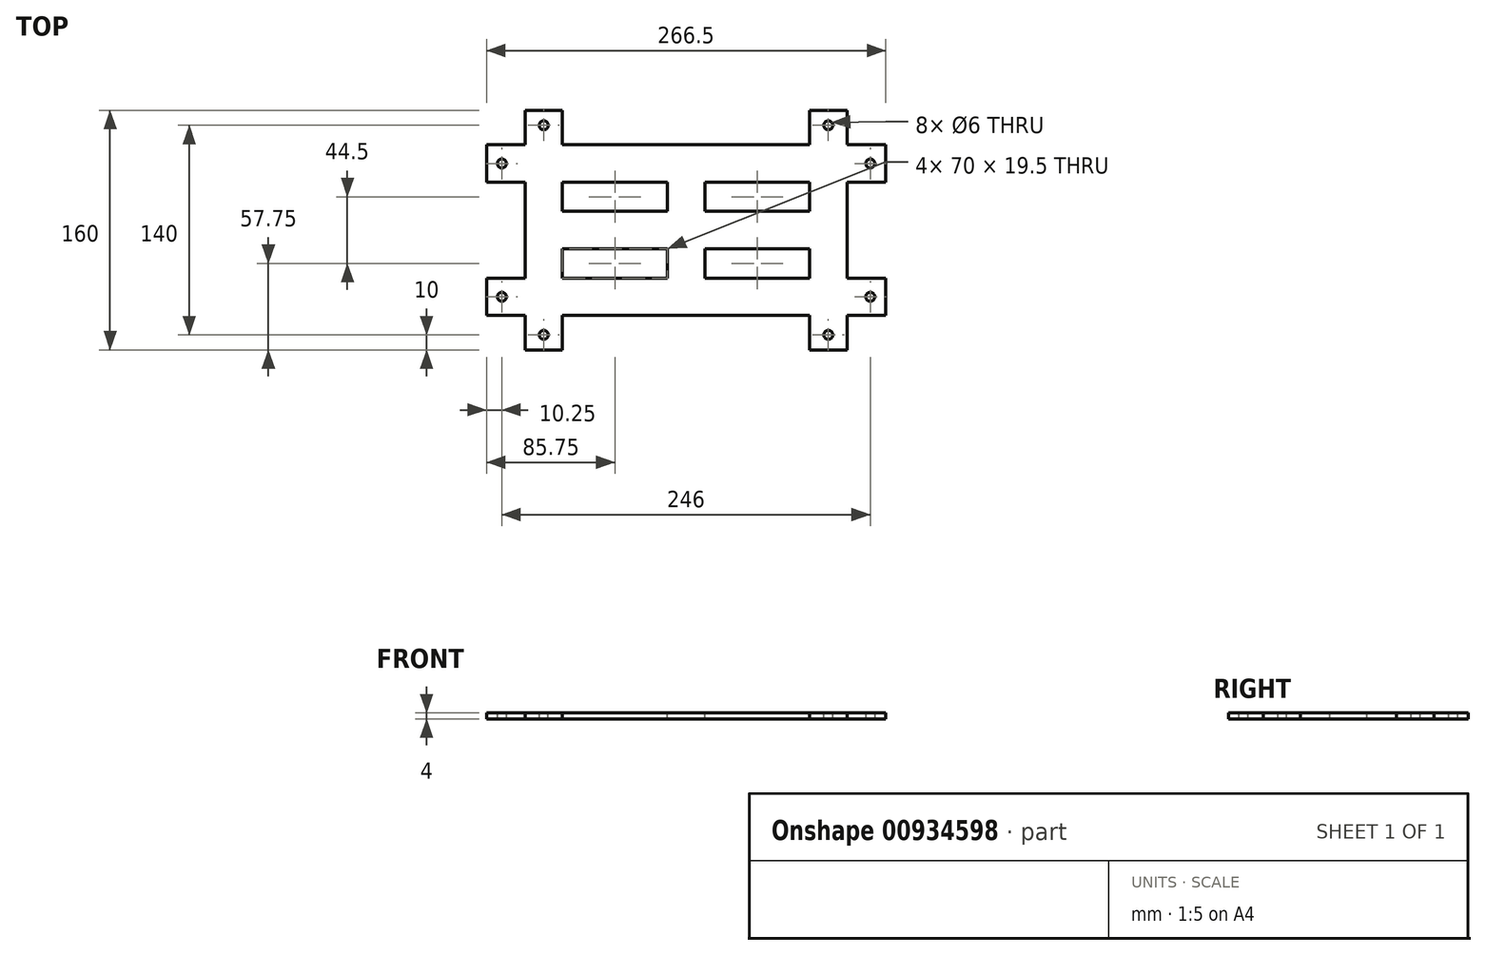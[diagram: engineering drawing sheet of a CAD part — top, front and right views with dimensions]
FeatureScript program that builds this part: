
annotation { "Feature Type Name" : "Feature", "Feature Type Description" : "" }
export const myFeature = defineFeature(function(context is Context, id is Id, definition is map)
    precondition{}
    {
        {
            var Q0;
            Q0=qCreatedBy(makeId("Top.planeOp"),FACE);
            var sketch = newSketch(context, id + "F0", { "sketchPlane" : qUnion([Q0])});
            skLineSegment(sketch, "E0.bottom", {"start": v(-133.25, 80) * mm, "end": v(133.25, 80) * mm});
            skLineSegment(sketch, "E0.top", {"start": v(-133.25, -80) * mm, "end": v(133.25, -80) * mm});
            skLineSegment(sketch, "E0.left", {"start": v(-133.25, 80) * mm, "end": v(-133.25, -80) * mm});
            skLineSegment(sketch, "E0.right", {"start": v(133.25, 80) * mm, "end": v(133.25, -80) * mm});
            skCircle(sketch, "E1", {"center": v(-123, 44.5) * mm, "radius": 3 * mm});
            skCircle(sketch, "E2", {"center": v(-123, -44.5) * mm, "radius": 3 * mm});
            skCircle(sketch, "E3", {"center": v(123, -44.5) * mm, "radius": 3 * mm});
            skCircle(sketch, "E4", {"center": v(123, 44.5) * mm, "radius": 3 * mm});
            skSolve(sketch);
        }
        {
            var Q0;
            Q0 = qSketchRegion(id + "F0", true);
            extrude(context, id + "F1", {"entities" : qUnion([Q0]), "depth" : 4 * mm, "offsetDistance" : 25 * mm});
        }
        {
            var Q0;
            Q0=makeQuery(id+"F1.opExtrude","CAP_FACE",FACE,{"disambiguationData":[OSD([sQuery(id+"F0.wireOp",EDGE,"E0.bottom"),sQuery(id+"F0.wireOp",EDGE,"E0.top"),sQuery(id+"F0.wireOp",EDGE,"E0.left"),sQuery(id+"F0.wireOp",EDGE,"E0.right"),sQuery(id+"F0.wireOp",EDGE,"E1"),sQuery(id+"F0.wireOp",EDGE,"E2"),sQuery(id+"F0.wireOp",EDGE,"E3"),sQuery(id+"F0.wireOp",EDGE,"E4")])],"isStart":false});
            var sketch = newSketch(context, id + "F2", { "sketchPlane" : qUnion([Q0])});
            skCircle(sketch, "E5", {"center": v(-95, 70) * mm, "radius": 3 * mm});
            skCircle(sketch, "E6", {"center": v(-95, -70) * mm, "radius": 3 * mm});
            skCircle(sketch, "E7.MirrorC", {"center": v(95, 70) * mm, "radius": 3 * mm});
            skCircle(sketch, "E8.MirrorC", {"center": v(95, -70) * mm, "radius": 3 * mm});
            skSolve(sketch);
        }
        {
            var Q0;
            Q0 = qSketchRegion(id + "F2", true);
            extrude(context, id + "F3", {"entities" : qUnion([Q0]), "operationType" : NewBodyOperationType.REMOVE, "endBound" : BoundingType.THROUGH_ALL, "oppositeDirection" : true, "depth" : 25 * mm, "offsetDistance" : 25 * mm});
        }
        {
            var Q0;
            Q0=makeQuery(id+"F1.opExtrude","CAP_FACE",FACE,{"disambiguationData":[OSD([sQuery(id+"F0.wireOp",EDGE,"E0.bottom"),sQuery(id+"F0.wireOp",EDGE,"E0.top"),sQuery(id+"F0.wireOp",EDGE,"E0.left"),sQuery(id+"F0.wireOp",EDGE,"E0.right"),sQuery(id+"F0.wireOp",EDGE,"E1"),sQuery(id+"F0.wireOp",EDGE,"E2"),sQuery(id+"F0.wireOp",EDGE,"E3"),sQuery(id+"F0.wireOp",EDGE,"E4")])],"isStart":false});
            var sketch = newSketch(context, id + "F4", { "sketchPlane" : qUnion([Q0])});
            skLineSegment(sketch, "E9.bottom", {"start": v(-133.25, 80) * mm, "end": v(-107.5, 80) * mm});
            skLineSegment(sketch, "E9.top", {"start": v(-133.25, 57) * mm, "end": v(-107.5, 57) * mm});
            skLineSegment(sketch, "E9.left", {"start": v(-133.25, 80) * mm, "end": v(-133.25, 57) * mm});
            skLineSegment(sketch, "E9.right", {"start": v(-107.5, 80) * mm, "end": v(-107.5, 57) * mm});
            skLineSegment(sketch, "E10.bottom", {"start": v(-82.5, 80) * mm, "end": v(0, 80) * mm});
            skLineSegment(sketch, "E10.top", {"start": v(-82.5, 57) * mm, "end": v(0, 57) * mm});
            skLineSegment(sketch, "E10.left", {"start": v(-82.5, 80) * mm, "end": v(-82.5, 57) * mm});
            skLineSegment(sketch, "E10.right", {"start": v(0, 80) * mm, "end": v(0, 57) * mm});
            skLineSegment(sketch, "E11.bottom", {"start": v(-107.5, 32) * mm, "end": v(-133.25, 32) * mm});
            skLineSegment(sketch, "E11.top", {"start": v(-107.5, 0) * mm, "end": v(-133.25, 0) * mm});
            skLineSegment(sketch, "E11.left", {"start": v(-107.5, 32) * mm, "end": v(-107.5, 0) * mm});
            skLineSegment(sketch, "E11.right", {"start": v(-133.25, 32) * mm, "end": v(-133.25, 0) * mm});
            skLineSegment(sketch, "E12.MirrorCS", {"start": v(133.25, 80) * mm, "end": v(133.25, 57) * mm});
            skLineSegment(sketch, "E13.MirrorCS", {"start": v(82.5, 57) * mm, "end": v(0, 57) * mm});
            skLineSegment(sketch, "E14.MirrorCS", {"start": v(133.25, 57) * mm, "end": v(107.5, 57) * mm});
            skLineSegment(sketch, "E15.MirrorCS", {"start": v(82.5, 80) * mm, "end": v(0, 80) * mm});
            skLineSegment(sketch, "E16.MirrorCS", {"start": v(107.5, 80) * mm, "end": v(107.5, 57) * mm});
            skLineSegment(sketch, "E17.MirrorCS", {"start": v(133.25, 80) * mm, "end": v(107.5, 80) * mm});
            skLineSegment(sketch, "E18.MirrorCS", {"start": v(82.5, 80) * mm, "end": v(82.5, 57) * mm});
            skLineSegment(sketch, "E19.MirrorCS", {"start": v(133.25, 32) * mm, "end": v(133.25, 0) * mm});
            skLineSegment(sketch, "E20.MirrorCS", {"start": v(107.5, 32) * mm, "end": v(133.25, 32) * mm});
            skLineSegment(sketch, "E21.MirrorCS", {"start": v(107.5, 32) * mm, "end": v(107.5, 0) * mm});
            skLineSegment(sketch, "E22.MirrorCS", {"start": v(107.5, 0) * mm, "end": v(133.25, 0) * mm});
            skLineSegment(sketch, "E23.MirrorCS", {"start": v(0, -80) * mm, "end": v(0, -57) * mm});
            skLineSegment(sketch, "E24.MirrorCS", {"start": v(107.5, -32) * mm, "end": v(107.5, 0) * mm});
            skLineSegment(sketch, "E25.MirrorCS", {"start": v(-133.25, -80) * mm, "end": v(-107.5, -80) * mm});
            skLineSegment(sketch, "E26.MirrorCS", {"start": v(133.25, -80) * mm, "end": v(133.25, -57) * mm});
            skLineSegment(sketch, "E27.MirrorCS", {"start": v(107.5, -32) * mm, "end": v(133.25, -32) * mm});
            skLineSegment(sketch, "E28.MirrorCS", {"start": v(82.5, -80) * mm, "end": v(82.5, -57) * mm});
            skLineSegment(sketch, "E29.MirrorCS", {"start": v(-133.25, -80) * mm, "end": v(-133.25, -57) * mm});
            skLineSegment(sketch, "E30.MirrorCS", {"start": v(82.5, -57) * mm, "end": v(0, -57) * mm});
            skLineSegment(sketch, "E31.MirrorCS", {"start": v(133.25, -80) * mm, "end": v(107.5, -80) * mm});
            skLineSegment(sketch, "E32.MirrorCS", {"start": v(107.5, -80) * mm, "end": v(107.5, -57) * mm});
            skLineSegment(sketch, "E33.MirrorCS", {"start": v(-133.25, -32) * mm, "end": v(-133.25, 0) * mm});
            skLineSegment(sketch, "E34.MirrorCS", {"start": v(-107.5, -80) * mm, "end": v(-107.5, -57) * mm});
            skLineSegment(sketch, "E35.MirrorCS", {"start": v(-82.5, -80) * mm, "end": v(-82.5, -57) * mm});
            skLineSegment(sketch, "E36.MirrorCS", {"start": v(-133.25, -57) * mm, "end": v(-107.5, -57) * mm});
            skLineSegment(sketch, "E37.MirrorCS", {"start": v(-82.5, -57) * mm, "end": v(0, -57) * mm});
            skLineSegment(sketch, "E38.MirrorCS", {"start": v(-82.5, -80) * mm, "end": v(0, -80) * mm});
            skLineSegment(sketch, "E39.MirrorCS", {"start": v(-107.5, -32) * mm, "end": v(-133.25, -32) * mm});
            skLineSegment(sketch, "E40.MirrorCS", {"start": v(82.5, -80) * mm, "end": v(0, -80) * mm});
            skLineSegment(sketch, "E41.MirrorCS", {"start": v(-107.5, -32) * mm, "end": v(-107.5, 0) * mm});
            skLineSegment(sketch, "E42.MirrorCS", {"start": v(133.25, -32) * mm, "end": v(133.25, 0) * mm});
            skLineSegment(sketch, "E43.MirrorCS", {"start": v(133.25, -57) * mm, "end": v(107.5, -57) * mm});
            skSolve(sketch);
        }
        {
            var Q0;
            Q0 = qSketchRegion(id + "F4", true);
            extrude(context, id + "F5", {"entities" : qUnion([Q0]), "operationType" : NewBodyOperationType.REMOVE, "endBound" : BoundingType.THROUGH_ALL, "oppositeDirection" : true, "depth" : 25 * mm, "offsetDistance" : 25 * mm});
        }
        {
            var Q0;
            Q0=makeQuery(id+"F1.opExtrude","CAP_FACE",FACE,{"disambiguationData":[OSD([sQuery(id+"F0.wireOp",EDGE,"E0.bottom"),sQuery(id+"F0.wireOp",EDGE,"E0.top"),sQuery(id+"F0.wireOp",EDGE,"E0.left"),sQuery(id+"F0.wireOp",EDGE,"E0.right"),sQuery(id+"F0.wireOp",EDGE,"E1"),sQuery(id+"F0.wireOp",EDGE,"E2"),sQuery(id+"F0.wireOp",EDGE,"E3"),sQuery(id+"F0.wireOp",EDGE,"E4")])],"isStart":false});
            var sketch = newSketch(context, id + "F6", { "sketchPlane" : qUnion([Q0])});
            skLineSegment(sketch, "E44.bottom", {"start": v(-82.5, 32) * mm, "end": v(-12.5, 32) * mm});
            skLineSegment(sketch, "E44.top", {"start": v(-82.5, 12.5) * mm, "end": v(-12.5, 12.5) * mm});
            skLineSegment(sketch, "E44.left", {"start": v(-82.5, 32) * mm, "end": v(-82.5, 12.5) * mm});
            skLineSegment(sketch, "E44.right", {"start": v(-12.5, 32) * mm, "end": v(-12.5, 12.5) * mm});
            skLineSegment(sketch, "E45.MirrorCS", {"start": v(82.5, 32) * mm, "end": v(12.5, 32) * mm});
            skLineSegment(sketch, "E46.MirrorCS", {"start": v(12.5, 32) * mm, "end": v(12.5, 12.5) * mm});
            skLineSegment(sketch, "E47.MirrorCS", {"start": v(82.5, 12.5) * mm, "end": v(12.5, 12.5) * mm});
            skLineSegment(sketch, "E48.MirrorCS", {"start": v(82.5, 32) * mm, "end": v(82.5, 12.5) * mm});
            skLineSegment(sketch, "E49.MirrorCS", {"start": v(82.5, -12.5) * mm, "end": v(12.5, -12.5) * mm});
            skLineSegment(sketch, "E50.MirrorCS", {"start": v(-82.5, -32) * mm, "end": v(-82.5, -12.5) * mm});
            skLineSegment(sketch, "E51.MirrorCS", {"start": v(-82.5, -32) * mm, "end": v(-12.5, -32) * mm});
            skLineSegment(sketch, "E52.MirrorCS", {"start": v(-82.5, -12.5) * mm, "end": v(-12.5, -12.5) * mm});
            skLineSegment(sketch, "E53.MirrorCS", {"start": v(12.5, -32) * mm, "end": v(12.5, -12.5) * mm});
            skLineSegment(sketch, "E54.MirrorCS", {"start": v(82.5, -32) * mm, "end": v(12.5, -32) * mm});
            skLineSegment(sketch, "E55.MirrorCS", {"start": v(-12.5, -32) * mm, "end": v(-12.5, -12.5) * mm});
            skLineSegment(sketch, "E56.MirrorCS", {"start": v(82.5, -32) * mm, "end": v(82.5, -12.5) * mm});
            skSolve(sketch);
        }
        {
            var Q0;
            Q0 = qSketchRegion(id + "F6", true);
            extrude(context, id + "F7", {"entities" : qUnion([Q0]), "operationType" : NewBodyOperationType.REMOVE, "endBound" : BoundingType.THROUGH_ALL, "oppositeDirection" : true, "depth" : 25 * mm, "offsetDistance" : 25 * mm});
        }
    });
